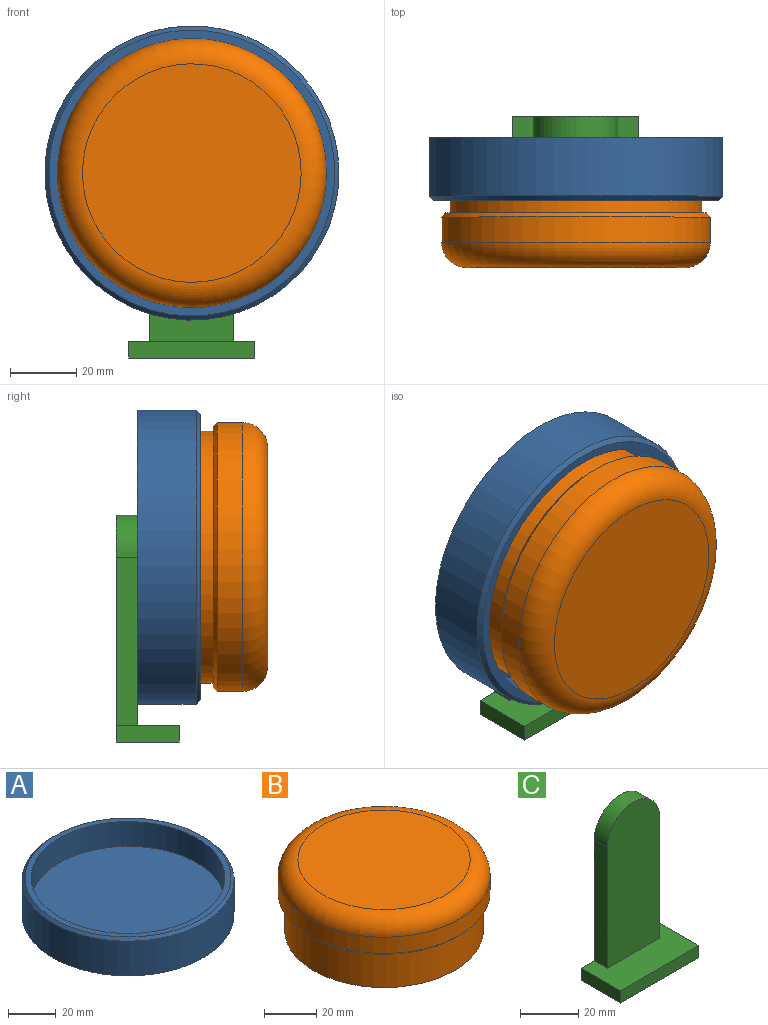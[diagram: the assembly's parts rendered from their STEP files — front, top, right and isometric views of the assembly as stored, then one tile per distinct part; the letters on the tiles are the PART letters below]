
ASSEMBLY  parts=3 mates=2
PART A: 6 faces, bbox 88.9x88.9x19.1 mm
  f0: cylinder r=44.45mm len=88.9mm, axis (0,0,-1), area 4965.7mm2, adj f2,f5
  f1: plane 86.36x86.36mm, normal (0,0,1), area 668.9mm2, adj f3,f5
  f2: plane 88.9x88.9mm, normal (0,0,-1), area 6207.2mm2, adj f0
  f3: cylinder r=40.64mm len=81.28mm, axis (0,0,1), area 3242.9mm2, adj f1,f4
  f4: plane 81.28x81.28mm, normal (0,0,1), area 5188.7mm2, adj f3
  f5: cone r=43.18mm half-angle=45deg, axis (0,0,-1), area 494.4mm2, adj f0,f1
PART B: 7 faces, bbox 88x88x33 mm
  f0: cylinder r=38.1mm len=76.2mm, axis (0,0,-1), area 3952.3mm2, adj f1,f4
  f1: plane 76.2x76.2mm, normal (0,0,-1), area 4560.4mm2, adj f0
  f2: cylinder r=40.64mm len=81.28mm, axis (0,0,-1), area 1945.8mm2, adj f5,f6
  f3: plane 66.04x66.04mm, normal (0,0,1), area 3425.3mm2, adj f5
  f4: plane 78.74x78.74mm, normal (0,0,-1), area 309.1mm2, adj f0,f6
  f5: torus R=33.02mm, axis (0,0,1), area 2848.1mm2, adj f2,f3
  f6: cone r=40.64mm half-angle=45deg, axis (0,0,1), area 451.5mm2, adj f2,f4
PART C: 10 faces, bbox 38.1x19.1x68.6 mm
  f0: plane 38.1x19.05mm, normal (0,0,1), area 564.5mm2, adj f1,f2,f3,f4,f6,f7,f8
  f1: plane 19.05x5.08mm, normal (-1,0,0), area 96.8mm2, adj f0,f2,f4,f5
  f2: plane 38.1x5.08mm, normal (0,-1,0), area 193.5mm2, adj f0,f1,f3,f5
  f3: plane 19.05x5.08mm, normal (1,0,0), area 96.8mm2, adj f0,f2,f4,f5
  f4: plane 68.58x38.1mm, normal (0,1,0), area 1737.2mm2, adj f0,f1,f3,f5,f6,f7,f9
  f5: plane 38.1x19.05mm, normal (0,0,-1), area 725.8mm2, adj f1,f2,f3,f4
  f6: plane 50.8x6.35mm, normal (1,0,0), area 322.6mm2, adj f0,f4,f8,f9
  f7: plane 50.8x6.35mm, normal (-1,0,0), area 322.6mm2, adj f0,f4,f8,f9
  f8: plane 63.5x25.4mm, normal (0,-1,0), area 1543.7mm2, adj f0,f6,f7,f9
  f9: cylinder r=12.7mm len=25.4mm, axis (0,-1,0), area 253.4mm2, adj f4,f6,f7,f8
PLACE A rot(axis=(1,0,0),90deg) t=(-99.95,-57.44,57.46)mm
PLACE B rot(axis=(1,0,0),90deg) t=(-99.95,-57.44,57.46)mm
PLACE C t=(-43.54,5.34,6.66)mm
MATE fastened A.f0 <-> B.f0  axis (0,-1,0) through (-99.95,-63.79,57.46)mm
MATE fastened A.f0 <-> C.f9  axis (0,1,0) through (-99.95,-57.44,57.46)mm
